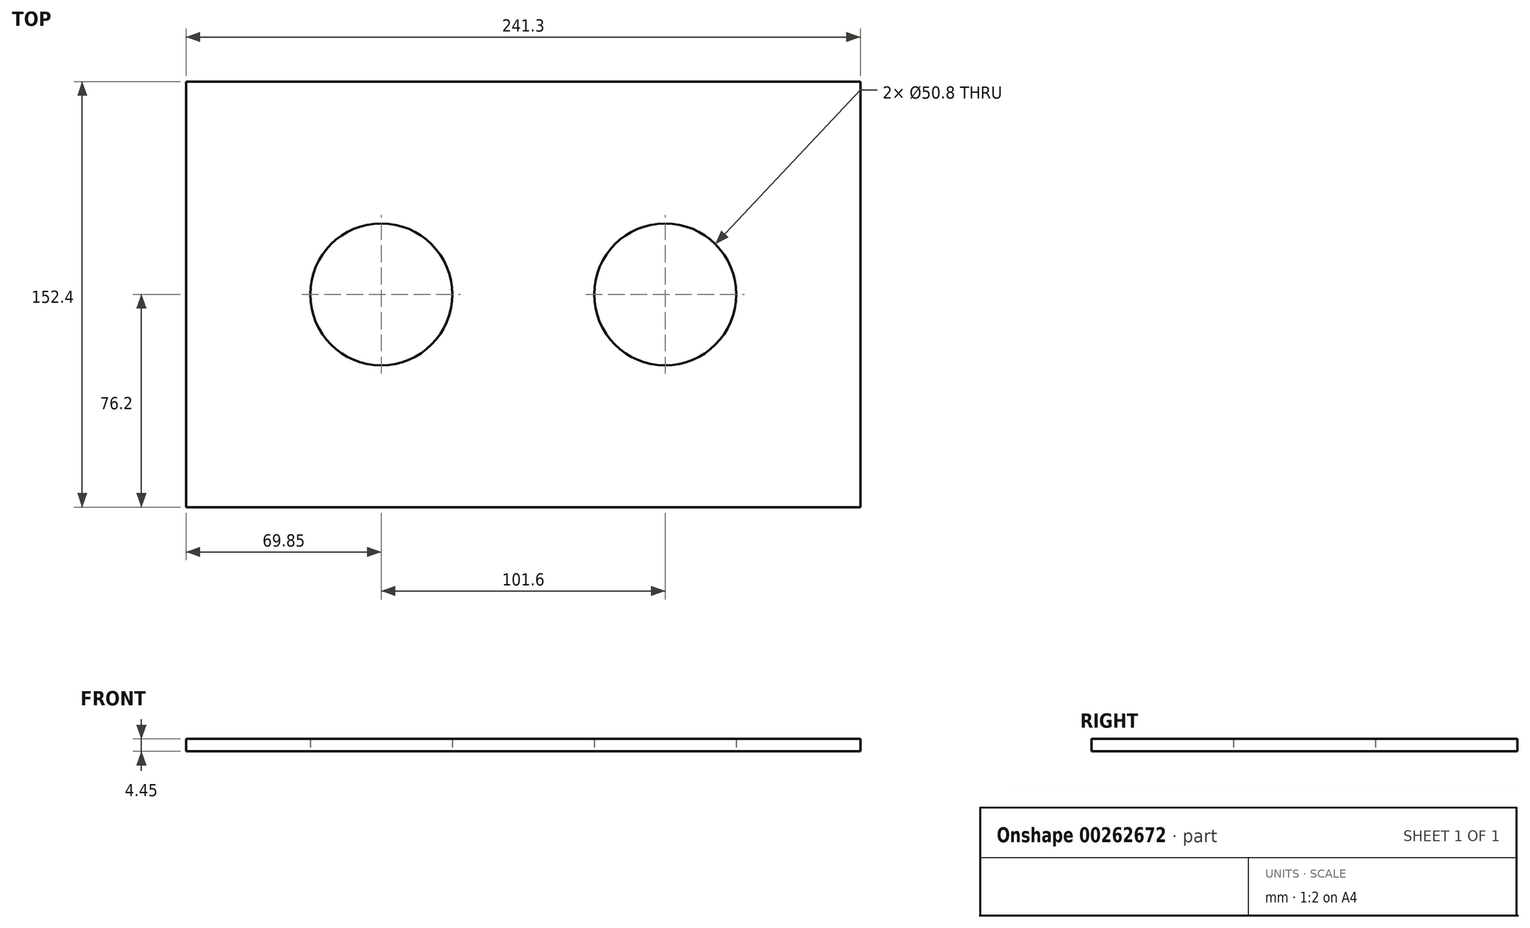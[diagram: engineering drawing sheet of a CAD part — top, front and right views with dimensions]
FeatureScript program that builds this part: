
annotation { "Feature Type Name" : "Feature", "Feature Type Description" : "" }
export const myFeature = defineFeature(function(context is Context, id is Id, definition is map)
    precondition{}
    {
        {
            var Q0;
            Q0=qCreatedBy(makeId("Top.planeOp"),FACE);
            var sketch = newSketch(context, id + "F0", { "sketchPlane" : qUnion([Q0])});
            skLineSegment(sketch, "E0.bottom", {"start": v(0, 0) * mm, "end": v(241.3, 0) * mm});
            skLineSegment(sketch, "E0.top", {"start": v(0, 152.4) * mm, "end": v(241.3, 152.4) * mm});
            skLineSegment(sketch, "E0.left", {"start": v(0, 0) * mm, "end": v(0, 152.4) * mm});
            skLineSegment(sketch, "E0.right", {"start": v(241.3, 0) * mm, "end": v(241.3, 152.4) * mm});
            skCircle(sketch, "E1", {"center": v(69.85, 76.2) * mm, "radius": 25.4 * mm});
            skPoint(sketch, "E1.centerSnap0", {"position": v(0, 76.2) * mm});
            skCircle(sketch, "E2", {"center": v(171.45, 76.2) * mm, "radius": 25.4 * mm});
            skSolve(sketch);
        }
        {
            var Q0;
            Q0=makeQuery(id+"F0.imprint","IMPRINT",FACE,{"disambiguationData":[TD([[makeQuery(id+"F0.imprint","IMPRINT",EDGE,{"derivedFrom":sQuery(id+"F0.wireOp",EDGE,"E0.bottom")}),1.0]])]});
            extrude(context, id + "F1", {"entities" : qUnion([Q0]), "depth" : 4.44 * mm});
        }
    });
